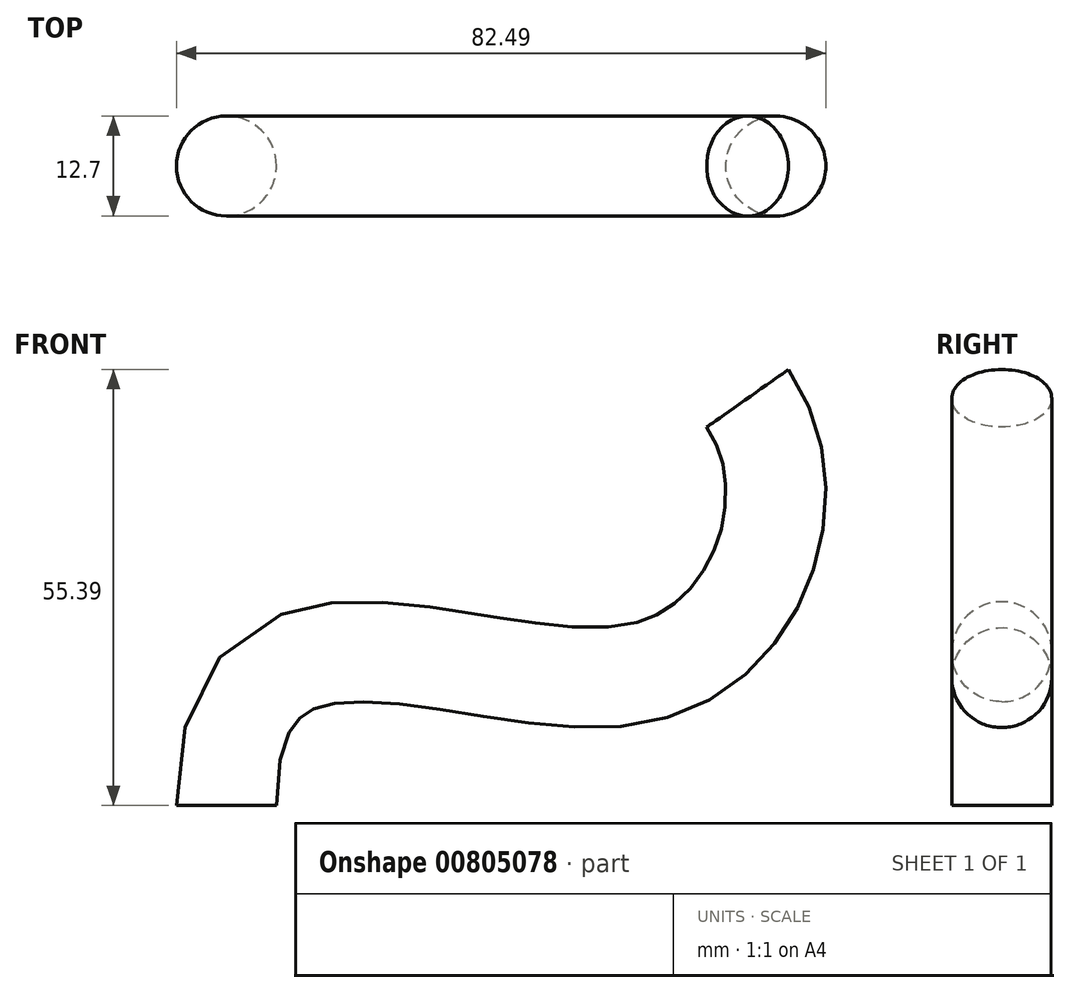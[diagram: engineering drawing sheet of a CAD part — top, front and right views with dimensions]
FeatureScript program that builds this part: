
annotation { "Feature Type Name" : "Feature", "Feature Type Description" : "" }
export const myFeature = defineFeature(function(context is Context, id is Id, definition is map)
    precondition{}
    {
        {
            var Q0;
            Q0=qCreatedBy(makeId("Top.planeOp"),FACE);
            var sketch = newSketch(context, id + "F0", { "sketchPlane" : qUnion([Q0])});
            skCircle(sketch, "E0", {"center": v(0, 0) * mm, "radius": 6.35 * mm});
            skSolve(sketch);
        }
        {
            var Q0;
            Q0=qCreatedBy(makeId("Front.planeOp"),FACE);
            var sketch = newSketch(context, id + "F1", { "sketchPlane" : qUnion([Q0])});
            skLineSegment(sketch, "E1", {"start": v(0, 0) * mm, "end": v(0, 33.55) * mm, "construction": true});
            skLineSegment(sketch, "E2", {"start": v(0, 33.55) * mm, "end": v(66.2, 51.73) * mm, "construction": true});
            skPoint(sketch, "E3.1.internal.snap0", {"position": v(0, 16.77) * mm});
            skFitSpline(sketch, "E3", {"points": [v(0, 0) * mm, v(52.33, 16.77) * mm, v(66.2, 51.73) * mm], "startDerivative": vector(0, 183.9) * mm, "endDerivative": vector(-54.1, 76.72) * mm});
            skSolve(sketch);
        }
        {
            var Q0;
            Q0 = qSketchRegion(id + "F0", true);
            var Q1;
            Q1 = qConstructionFilter(qBodyType(qCreatedBy(id + "F1" ,EDGE), BodyType.WIRE), ConstructionObject.NO);
            sweep(context, id + "F2", {"profiles" : qUnion([Q0]), "path" : qUnion([Q1])});
        }
    });
